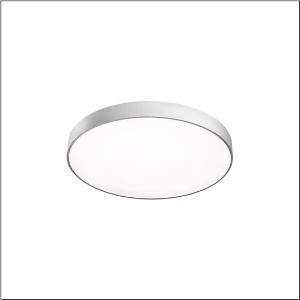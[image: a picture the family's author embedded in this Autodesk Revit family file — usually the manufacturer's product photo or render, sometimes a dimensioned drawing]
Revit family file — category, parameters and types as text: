
# Revit family: round_21_m_51mr36fm8421s
name_source: partatom
category: Lighting Fixtures
units: mm (PartAtom-declared; Revit-internal decimal feet)

## family parameters
Cut with Voids When Loaded = No
Host = Face
Light Source = No
Part Type = Normal
Room Calculation Point = No
Round Connector Dimension = Use Diameter
Shared = No

## types (1)
- --- (1 x LED, 8140 lm, 61.1 W, 4000K)
    Apparent Load = 61 VA
    CIE Flux Codes = 49 80 96 100 100
    Color Rendering = 80
    Color Temperature = 4000K
    Default Elevation = 1800 mm
    Description = Round 21 M, wall and ceiling luminaire, primary optical cover: cover, of PMMA, opal, light emission: direct distribution, primary light characteristic: symmetric, installation type: suspended mounting, surface-mounted, LED, rated luminous flux: 8.140lm, luminous efficacy: 133lm/W, light colour: 840, colour temperature: 4000K, with terminal, 3-pole, mains connection: 230V, AC, 50/60Hz, rated input power: 61W, housing, of aluminium, coated, silver, diameter: 600mm, height: 62mm, protection rating (complete): IP40, insulation class (complete): insulation class I (protective earthing), certification: CE, impact resistance: IK04, permissible operating ambient temperature: -10..+35°C, packaging unit: 1 piece
    Height = 87 mm
    Lamp = 1 x LED
    Lamp Light Flux = 8140 lm
    Lamp Power = 61.1 W
    Lamp count = 1
    Length = 600 mm
    Luminous efficacy = 133 lm/W
    Manufacturer = Siteco
    ModVariant = No
    Model = 51MR36FM8421S
    Mounting Place = Ceiling
    Mounting Type = Surface mounted
    Number of Poles = 1
    OnlyDefault = Yes
    Power Factor = 1
    Product Name = Round 21 M
    Product group = wall and ceiling luminaire
    ProductGroupID = 301
    Protection Class = Protection class I
    Protection Degree = IP 40
    RLX_Detail_Level = 1
    RLX_Emergency_Light_Flux = 0 lm
    RLX_Emergency_Type = 0
    RLX_Emergency_Type_DB = No
    RlxData = <blob elided: 17373 chars, md5=932a7c7a>
    Socket = socket
    Standby Power = 0 W
    System Light Flux = 8140 lm
    System Power = 61 W
    Type Comments = factory setting: luminous flux: 100 % | (ON | ON | ON | ON) | 700 mA
    Type Image = l_1258303.jpg
    URL = http://relux.com
    VarID = @adj_013337
    Voltage = 0 V
    Weight = 0.00 kg
    Width = 0 mm  [stored 0 ft]

note: [stored X ft] marks values corroborated as IEEE doubles in the binary element streams (Revit-internal decimal feet)

## geometry (parser evidence)
native form markers: Blend x4, Sweep x11
no freeform markers — native parametric forms only
